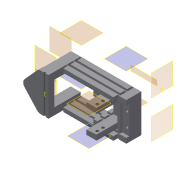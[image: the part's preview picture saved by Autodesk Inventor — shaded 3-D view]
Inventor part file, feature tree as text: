
AUTODESK INVENTOR PART (.ipt)
format: ipt  version: 2019.4 (Build 234330000, 330)  size: 568,832 bytes
history: native  units: mm
features: sketch x16, plane x15, extrude x15, projected_geometry x13, other x2, mirror x1, fillet x1
ambient origin geometry x8: Origin, YZ Plane, XZ Plane, XY Plane, X Axis, Y Axis, Z Axis, Center Point
bodies: Solid1 (feature_tree)
feature tree (63):
  plane  "Work Plane1"
  plane  "Work Plane2"
  plane  "Work Plane4"
  extrude  "Extrusion4"  Depth=4.0mm TaperAngle=0.0deg
  plane  "Work Plane5"
  extrude  "Extrusion5"  Depth=5.0mm TaperAngle=0.0deg
  plane  "Work Plane11"
  extrude  "Extrusion8"  Depth=5.0mm
  plane  "Work Plane7"
  extrude  "Extrusion9"  Depth=2.0mm
  plane  "Work Plane3"
  plane  "Work Plane13"
  extrude  "Extrusion10"  Depth=0.6mm
  plane  "Work Plane12"
  extrude  "Extrusion11"  Depth=4.0mm
  extrude  "Extrusion14"  Depth=1.0mm
  extrude  "Extrusion15"  Depth=2.9mm
  mirror  "Mirror2"
  extrude  "Extrusion17"  TaperAngle=0.0deg  [1 undecoded]
  extrude  "Extrusion18"  TaperAngle=0.0deg  [1 undecoded]
  sketch  "Sketch20"  dims[d101=7.0mm d102=0.0mm]
  extrude  "Extrusion19"  TaperAngle=0.0deg  [1 undecoded]
  extrude  "Extrusion20"  Depth=10.0mm
  fillet  "Fillet1"  Radius=22.0mm
  extrude  "Extrusion21"  Depth=4.0mm
  extrude  "Extrusion22"  TaperAngle=0.0deg  [1 undecoded]
  extrude  "Extrusion23"  Depth=0.6mm
  sketch  "Sketch5"  dims[d28=15.0mm d29=0.0mm d37=4.0mm d38=0.0mm]
  sketch  "Sketch6"  dims[d43=7.0mm d60=5.0mm d61=0.0mm]
  sketch  "Sketch9"  dims[d62=4.0mm d63=5.0mm]
  sketch  "Sketch10"  dims[d64=9.0mm d65=0.0mm d66=2.0mm]
  sketch  "Sketch11"  dims[d67=0.6mm d68=0.6mm]
  projected_geometry  "Projected Loop9"
  sketch  "Sketch12"  dims[d70=15.0mm d71=0.0mm d72=4.0mm]
  projected_geometry  "Projected Loop10"
  sketch  "Sketch15"  dims[d73=0.0mm d77=1.0mm]
  projected_geometry  "Projected Loop13"
  projected_geometry  "Projected Loop14"
  projected_geometry  "Projected Loop15"
  sketch  "Sketch16"  dims[d78=2.9mm d79=2.9mm]
  projected_geometry  "Projected Loop16"
  plane  "Work Plane14"
  plane  "Work Plane15"
  plane  "Work Plane16"
  plane  "Work Plane17"
  plane  "Work Plane18"
  plane  "Work Plane19"
  sketch  "Sketch18"  dims[d80=4.0mm d81=0.0mm d92=0.0mm]
  sketch  "Sketch19"  dims[d93=5.0mm d94=0.0mm]
  sketch  "Sketch21"  dims[d104=10.0mm d105=0.0mm d106=19.0mm d107=22.0mm]
  projected_geometry  "Projected Loop17"
  projected_geometry  "Projected Loop18"
  projected_geometry  "Projected Loop19"
  sketch  "Sketch22"  dims[d108=28.0mm d109=4.0mm]
  projected_geometry  "Projected Loop20"
  sketch  "Sketch23"  dims[d110=4.0mm d111=0.0mm]
  projected_geometry  "Projected Loop21"
  sketch  "Sketch24"  dims[d112=2.0mm d113=0.6mm]
  projected_geometry  "Projected Loop22"
  sketch  "Sketch25"  dims[d115=5.0mm d117=2.9mm d118=7.0mm d119=10.0mm d120=0.0mm d121=4.0mm d122=5.0mm d123=0.6mm d124=2.0mm d125=2.0mm d130=10.0mm d131=0.0mm d132=1.0mm d133=0.0mm d134=30.0mm d135=8.0mm d136=0.0mm d137=0.0mm d138=10.0mm d139=0.0mm d140=5.0mm d141=30.0mm d143=7.0mm d144=10.0mm d146=10.0mm d148=17.0mm d149=0.0mm d150=16.0mm d151=0.0mm d152=0.0mm d153=5.0mm d154=10.0mm d155=0.0mm d156=5.0mm d157=0.0mm d158=2.0mm d159=10.0mm d160=0.0mm]
  projected_geometry  "Projected Loop23"
  other  "Assembly_Opentrons_Autofocus_v2.iam"
  other  "00_MGN12C, LINEAR GUIDE BLOCK:1"
note: 4 required parameter values undecoded (feature->parameter linkage not recoverable at this tier; creation-order binding heuristic only, values carry confidence <= 0.55)
